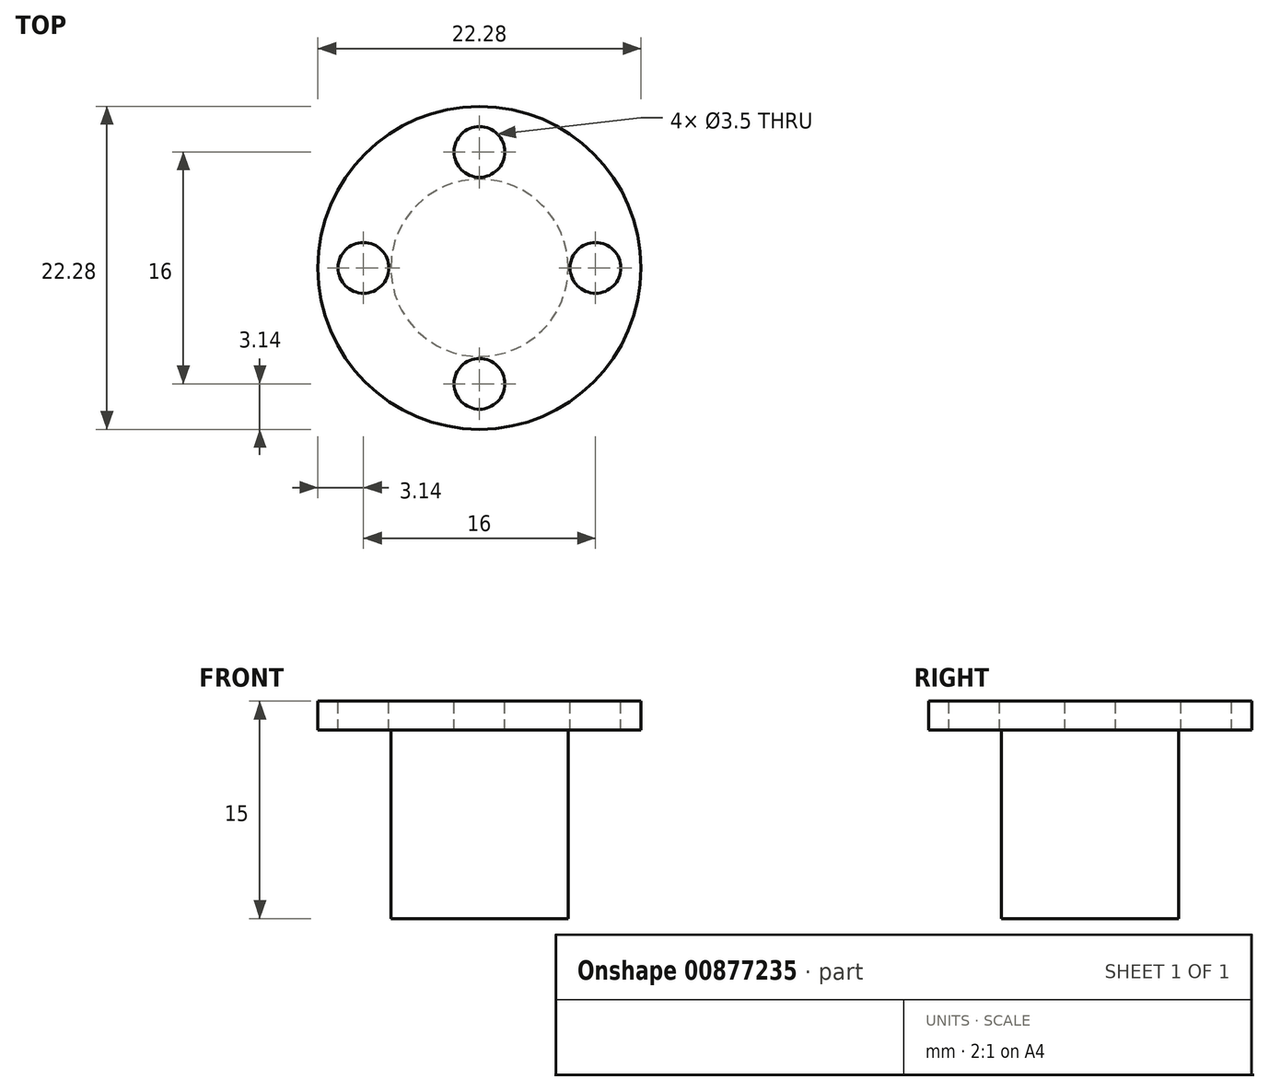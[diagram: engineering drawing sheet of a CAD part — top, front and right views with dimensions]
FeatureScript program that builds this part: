
annotation { "Feature Type Name" : "Feature", "Feature Type Description" : "" }
export const myFeature = defineFeature(function(context is Context, id is Id, definition is map)
    precondition{}
    {
        {
            var Q0;
            Q0=qCreatedBy(makeId("Front.planeOp"),FACE);
            var sketch = newSketch(context, id + "F0", { "sketchPlane" : qUnion([Q0])});
            skLineSegment(sketch, "E0", {"start": v(0, 0) * mm, "end": v(0, 15) * mm});
            skLineSegment(sketch, "E1", {"start": v(0, 15) * mm, "end": v(11.14, 15) * mm});
            skLineSegment(sketch, "E2", {"start": v(11.14, 15) * mm, "end": v(11.14, 13) * mm});
            skLineSegment(sketch, "E3", {"start": v(11.14, 13) * mm, "end": v(6.11, 13) * mm});
            skLineSegment(sketch, "E4", {"start": v(6.12, 13) * mm, "end": v(6.12, 0) * mm});
            skLineSegment(sketch, "E5", {"start": v(6.11, 0) * mm, "end": v(0, 0) * mm});
            skSolve(sketch);
        }
        {
            var Q0;
            Q0=makeQuery(id+"F0.imprint","IMPRINT",FACE,{"disambiguationData":[TD([[makeQuery(id+"F0.imprint","IMPRINT",EDGE,{"derivedFrom":sQuery(id+"F0.wireOp",EDGE,"E0")}),-1.0]])]});
            var Q1;
            Q1=sQuery(id+"F0.wireOp",EDGE,"E0");
            revolve(context, id + "F1", {"surfaceOperationType" : NewSurfaceOperationType.NEW, "entities" : qUnion([Q0]), "axis" : qUnion([Q1]), "revolveType" : RevolveType.FULL});
        }
        {
            var Q0;
            Q0=makeQuery(id+"F1.opRevolve","SWEPT_FACE",FACE,{"disambiguationData":[OSD([sQuery(id+"F0.wireOp",EDGE,"E1")])]});
            var sketch = newSketch(context, id + "F2", { "sketchPlane" : qUnion([Q0])});
            skCircle(sketch, "E6", {"center": v(0, 8) * mm, "radius": 1.75 * mm});
            skCircle(sketch, "E7", {"center": v(0, 0) * mm, "radius": 8 * mm});
            skCircle(sketch, "E8", {"center": v(8, 0) * mm, "radius": 1.75 * mm});
            skCircle(sketch, "E9", {"center": v(-8, 0) * mm, "radius": 1.75 * mm});
            skCircle(sketch, "E10", {"center": v(0, -8) * mm, "radius": 1.75 * mm});
            skSolve(sketch);
        }
        {
            var Q0;
            {var subQ0=sQuery(id+"F2.wireOp",EDGE,"E7");var subQ1=sQuery(id+"F2.wireOp",EDGE,"E6");var subQ2=makeQuery(id+"F2.imprint","INTERSECT",VERTEX,{"disambiguationData":[OD(0.0)],"derivedFrom":[subQ1,subQ0]});Q0=makeQuery(id+"F2.imprint","IMPRINT",FACE,{"disambiguationData":[TD([[makeQuery(id+"F2.imprint","IMPRINT",EDGE,{"disambiguationData":[TD([[subQ2,-1.0]])],"derivedFrom":subQ1}),1.0]])]});}
            var Q1;
            {var subQ0=sQuery(id+"F2.wireOp",EDGE,"E7");var subQ1=sQuery(id+"F2.wireOp",EDGE,"E6");var subQ2=makeQuery(id+"F2.imprint","INTERSECT",VERTEX,{"disambiguationData":[OD(0.0)],"derivedFrom":[subQ1,subQ0]});Q1=makeQuery(id+"F2.imprint","IMPRINT",FACE,{"disambiguationData":[TD([[makeQuery(id+"F2.imprint","IMPRINT",EDGE,{"disambiguationData":[TD([[subQ2,1.0]])],"derivedFrom":subQ1}),1.0]])]});}
            var Q2;
            {var subQ0=sQuery(id+"F2.wireOp",EDGE,"E9");var subQ1=sQuery(id+"F2.wireOp",EDGE,"E7");var subQ2=makeQuery(id+"F2.imprint","INTERSECT",VERTEX,{"disambiguationData":[OD(0.0)],"derivedFrom":[subQ1,subQ0]});Q2=makeQuery(id+"F2.imprint","IMPRINT",FACE,{"disambiguationData":[TD([[makeQuery(id+"F2.imprint","IMPRINT",EDGE,{"disambiguationData":[TD([[subQ2,-1.0]])],"derivedFrom":subQ1}),-1.0]])]});}
            var Q3;
            {var subQ0=sQuery(id+"F2.wireOp",EDGE,"E9");var subQ1=sQuery(id+"F2.wireOp",EDGE,"E7");var subQ2=makeQuery(id+"F2.imprint","INTERSECT",VERTEX,{"disambiguationData":[OD(0.0)],"derivedFrom":[subQ1,subQ0]});Q3=makeQuery(id+"F2.imprint","IMPRINT",FACE,{"disambiguationData":[TD([[makeQuery(id+"F2.imprint","IMPRINT",EDGE,{"disambiguationData":[TD([[subQ2,-1.0]])],"derivedFrom":subQ1}),1.0]])]});}
            var Q4;
            {var subQ0=sQuery(id+"F2.wireOp",EDGE,"E10");var subQ1=sQuery(id+"F2.wireOp",EDGE,"E7");var subQ2=makeQuery(id+"F2.imprint","INTERSECT",VERTEX,{"disambiguationData":[OD(0.0)],"derivedFrom":[subQ1,subQ0]});Q4=makeQuery(id+"F2.imprint","IMPRINT",FACE,{"disambiguationData":[TD([[makeQuery(id+"F2.imprint","IMPRINT",EDGE,{"disambiguationData":[TD([[subQ2,-1.0]])],"derivedFrom":subQ1}),1.0]])]});}
            var Q5;
            {var subQ0=sQuery(id+"F2.wireOp",EDGE,"E10");var subQ1=sQuery(id+"F2.wireOp",EDGE,"E7");var subQ2=makeQuery(id+"F2.imprint","INTERSECT",VERTEX,{"disambiguationData":[OD(0.0)],"derivedFrom":[subQ1,subQ0]});Q5=makeQuery(id+"F2.imprint","IMPRINT",FACE,{"disambiguationData":[TD([[makeQuery(id+"F2.imprint","IMPRINT",EDGE,{"disambiguationData":[TD([[subQ2,-1.0]])],"derivedFrom":subQ1}),-1.0]])]});}
            var Q6;
            {var subQ0=sQuery(id+"F2.wireOp",EDGE,"E8");var subQ1=sQuery(id+"F2.wireOp",EDGE,"E7");var subQ2=makeQuery(id+"F2.imprint","INTERSECT",VERTEX,{"disambiguationData":[OD(0.0)],"derivedFrom":[subQ1,subQ0]});Q6=makeQuery(id+"F2.imprint","IMPRINT",FACE,{"disambiguationData":[TD([[makeQuery(id+"F2.imprint","IMPRINT",EDGE,{"disambiguationData":[TD([[subQ2,1.0]])],"derivedFrom":subQ1}),-1.0]])]});}
            var Q7;
            {var subQ0=sQuery(id+"F2.wireOp",EDGE,"E8");var subQ1=sQuery(id+"F2.wireOp",EDGE,"E7");var subQ2=makeQuery(id+"F2.imprint","INTERSECT",VERTEX,{"disambiguationData":[OD(0.0)],"derivedFrom":[subQ1,subQ0]});Q7=makeQuery(id+"F2.imprint","IMPRINT",FACE,{"disambiguationData":[TD([[makeQuery(id+"F2.imprint","IMPRINT",EDGE,{"disambiguationData":[TD([[subQ2,1.0]])],"derivedFrom":subQ1}),1.0]])]});}
            extrude(context, id + "F3", {"entities" : qUnion([Q0, Q1, Q2, Q3, Q4, Q5, Q6, Q7]), "operationType" : NewBodyOperationType.REMOVE, "oppositeDirection" : true, "depth" : 5 * mm, "offsetDistance" : 25 * mm});
        }
    });
